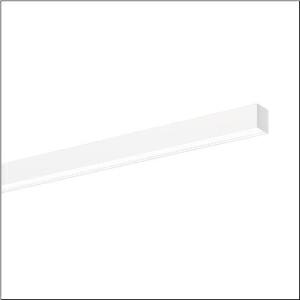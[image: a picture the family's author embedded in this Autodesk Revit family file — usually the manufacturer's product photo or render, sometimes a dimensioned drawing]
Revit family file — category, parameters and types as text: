
# Revit family: silica_r__21_51mx20dc45wb_dec1
name_source: partatom
category: Lighting Fixtures
units: mm (PartAtom-declared; Revit-internal decimal feet)

## family parameters
Cut with Voids When Loaded = No
Host = Face
Light Source = No
Part Type = Normal
Room Calculation Point = No
Round Connector Dimension = Use Diameter
Shared = No

## types (1)
- --- (1 x LED, 6000 lm, 40.1 W, 4000K)
    Apparent Load = 40 VA
    CIE Flux Codes = 48 79 96 100 100
    Color Rendering = 80
    Color Temperature = 4000K
    Default Elevation = 1800 mm
    Description = Silica® 21, office luminaire, primary optical cover: cover, of PMMA, opal, light emission: direct distribution, primary light characteristic: symmetric, installation type: surface-mounted, LED, rated luminous flux: 6.000lm, luminous efficacy: 150lm/W, light colour: 840, colour temperature: 4000K, with terminal, 3+2-pole, max. 2.5mm², mains connection: 220..240V, AC, 50/60Hz, rated input power: 40.1W, luminaire housing, of aluminium, traffic white (RAL 9016), length: 3.004mm, width: 53mm, height: 53mm, protection rating (complete): IP20, insulation class (complete): insulation class I (protective earthing), certification: CE, permissible operating ambient temperature: 0..+35°C, standard: EN 50419, packaging unit: 1 piece
    Height = 0 mm  [stored 0 ft]
    Lamp = 1 x LED
    Lamp Light Flux = 6000 lm
    Lamp Power = 40.1 W
    Lamp count = 1
    Length = 3004 mm
    Luminous efficacy = 150 lm/W
    Manufacturer = Siteco
    ModVariant = No
    Model = 51MX20DC45WB
    Mounting Place = Ceiling
    Mounting Type = Recessed
    Number of Poles = 1
    OnlyDefault = Yes
    Power Factor = 1
    Product Name = Silica® 21
    Product group = office luminaire | ceiling recessed
    ProductGroupID = 400
    Protection Class = Protection class I
    Protection Degree = IP 20
    RLX_Detail_Level = 1
    RLX_Emergency_Light_Flux = 0 lm
    RLX_Emergency_Type = 0
    RLX_Emergency_Type_DB = No
    RlxData = <blob elided: 23873 chars, md5=5e0712ac>
    Socket = socket
    Standby Power = 0 W
    System Light Flux = 6000 lm
    System Power = 40 W
    Type Comments = factory setting: luminous flux: 100 % | dim-lin: 254 | 218 mA
    Type Image = l_1335877.jpg
    URL = http://relux.com
    VarID = @adj_086813
    Voltage = 0 V
    Weight = 0.00 kg
    Width = 53 mm

note: [stored X ft] marks values corroborated as IEEE doubles in the binary element streams (Revit-internal decimal feet)

## geometry (parser evidence)
native form markers: Blend x4, Sweep x10
no freeform markers — native parametric forms only
